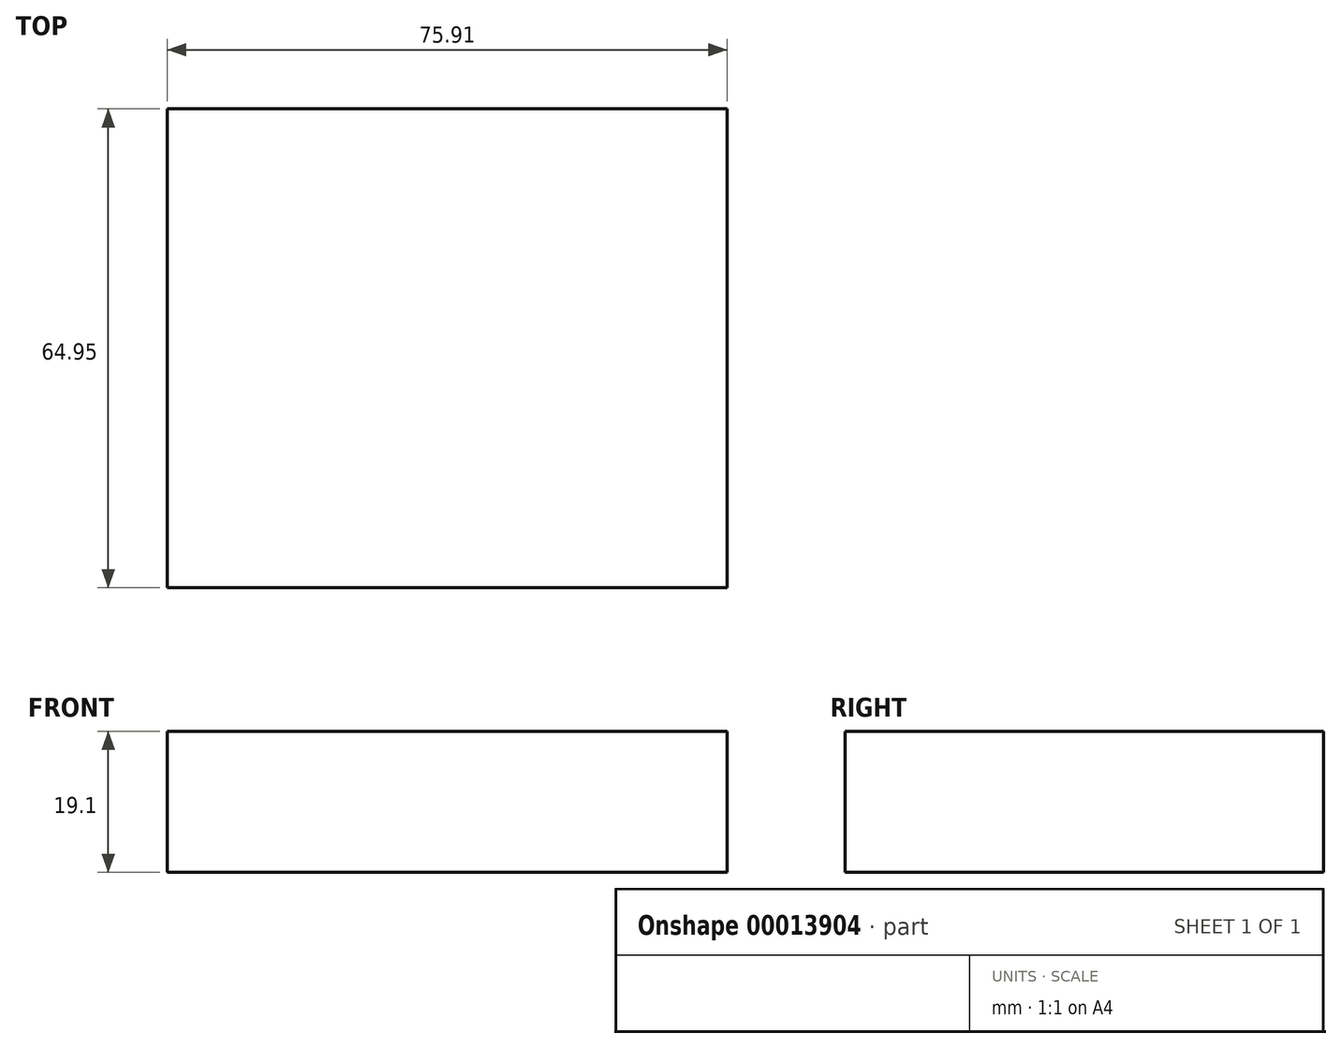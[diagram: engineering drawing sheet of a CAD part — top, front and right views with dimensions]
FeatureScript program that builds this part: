
annotation { "Feature Type Name" : "Feature", "Feature Type Description" : "" }
export const myFeature = defineFeature(function(context is Context, id is Id, definition is map)
    precondition{}
    {
        {
            var Q0;
            Q0=qCreatedBy(makeId("Top.planeOp"),FACE);
            var sketch = newSketch(context, id + "F0", { "sketchPlane" : qUnion([Q0])});
            skLineSegment(sketch, "E0.bottom", {"start": v(0, 0) * mm, "end": v(75.9, 0) * mm});
            skLineSegment(sketch, "E0.top", {"start": v(0, 64.95) * mm, "end": v(75.9, 64.95) * mm});
            skLineSegment(sketch, "E0.left", {"start": v(0, 0) * mm, "end": v(0, 64.95) * mm});
            skLineSegment(sketch, "E0.right", {"start": v(75.9, 0) * mm, "end": v(75.9, 64.95) * mm});
            skSolve(sketch);
        }
        {
            var Q0;
            Q0 = qSketchRegion(id + "F0", true);
            extrude(context, id + "F1", {"entities" : qUnion([Q0]), "oppositeDirection" : true, "depth" : 19.1 * mm});
        }
    });
